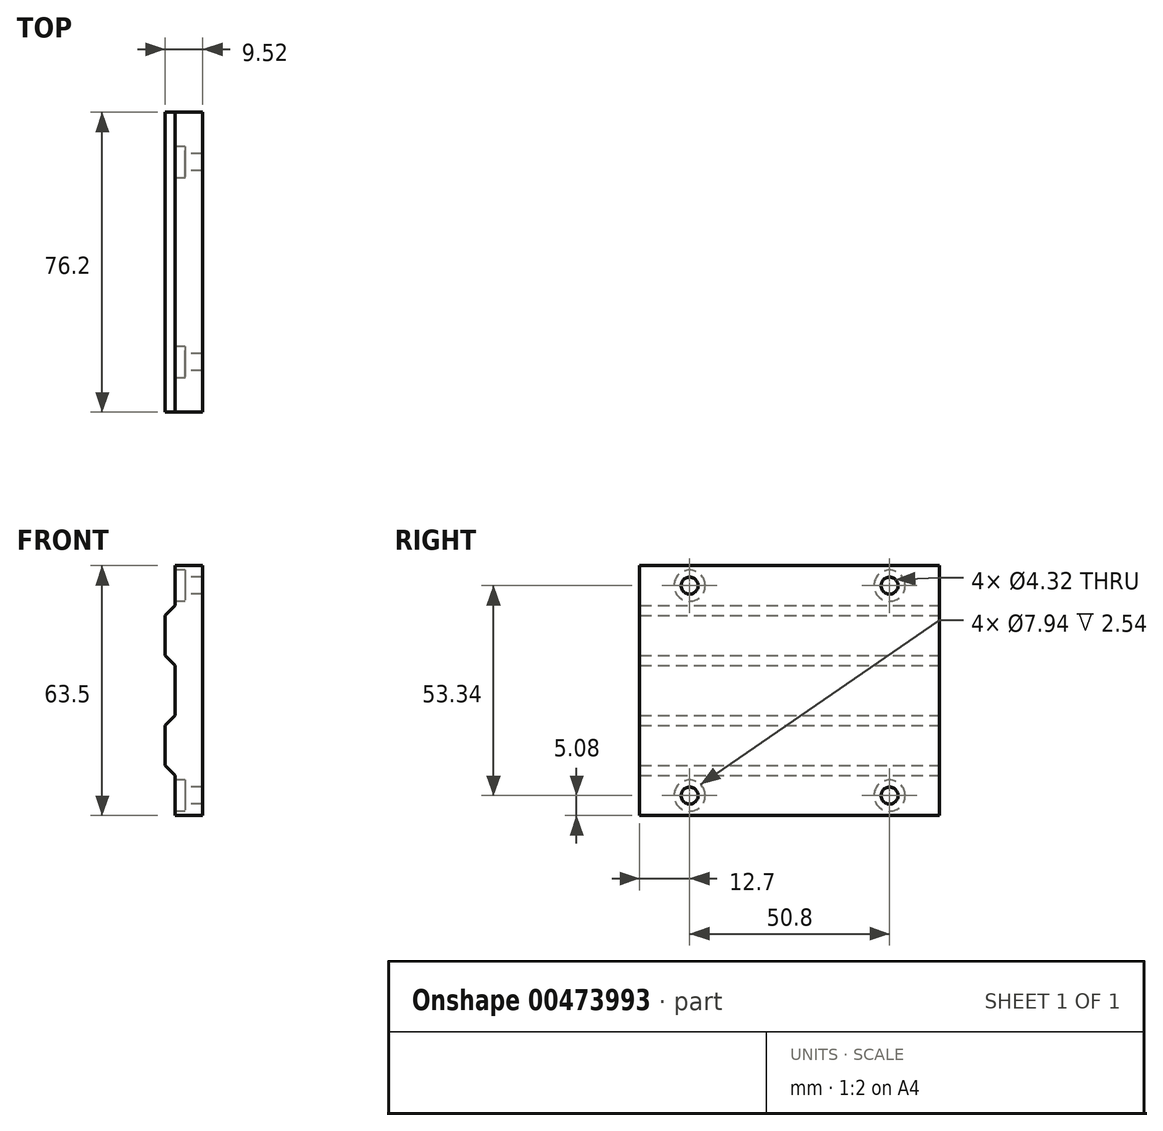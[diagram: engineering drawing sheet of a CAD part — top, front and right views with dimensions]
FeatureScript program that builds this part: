
annotation { "Feature Type Name" : "Feature", "Feature Type Description" : "" }
export const myFeature = defineFeature(function(context is Context, id is Id, definition is map)
    precondition{}
    {
        {
            var Q0;
            Q0=qCreatedBy(makeId("Front.planeOp"),FACE);
            var sketch = newSketch(context, id + "F0", { "sketchPlane" : qUnion([Q0])});
            skLineSegment(sketch, "E0.0.0", {"start": v(6.99, 40.64) * mm, "end": v(6.98, 50.8) * mm});
            skLineSegment(sketch, "E0.0.1", {"start": v(6.98, 50.8) * mm, "end": v(9.52, 53.34) * mm});
            skLineSegment(sketch, "E0.0.2", {"start": v(9.52, 53.34) * mm, "end": v(9.52, 63.5) * mm});
            skLineSegment(sketch, "E0.0.3", {"start": v(9.52, 63.5) * mm, "end": v(0, 63.5) * mm});
            skLineSegment(sketch, "E0.0.4", {"start": v(0, 63.5) * mm, "end": v(0, 0) * mm});
            skLineSegment(sketch, "E0.0.5", {"start": v(0, 0) * mm, "end": v(9.53, 0) * mm});
            skLineSegment(sketch, "E0.0.6", {"start": v(9.53, 0) * mm, "end": v(9.53, 10.16) * mm});
            skLineSegment(sketch, "E0.0.7", {"start": v(9.53, 10.16) * mm, "end": v(6.98, 12.7) * mm});
            skLineSegment(sketch, "E0.0.8", {"start": v(6.99, 12.7) * mm, "end": v(6.98, 22.86) * mm});
            skLineSegment(sketch, "E0.0.9", {"start": v(6.98, 22.86) * mm, "end": v(9.52, 25.4) * mm});
            skLineSegment(sketch, "E0.0.10", {"start": v(9.53, 25.4) * mm, "end": v(9.52, 38.1) * mm});
            skLineSegment(sketch, "E0.0.11", {"start": v(9.52, 38.1) * mm, "end": v(6.98, 40.64) * mm});
            skLineSegment(sketch, "E1", {"start": v(9.52, 63.5) * mm, "end": v(16.5, 63.5) * mm});
            skLineSegment(sketch, "E2", {"start": v(16.5, 63.5) * mm, "end": v(16.51, 0) * mm});
            skLineSegment(sketch, "E3", {"start": v(16.51, 0) * mm, "end": v(9.53, 0) * mm});
            skSolve(sketch);
        }
        {
            var Q0;
            Q0=makeQuery(id+"F0.imprint","IMPRINT",FACE,{"disambiguationData":[TD([[makeQuery(id+"F0.imprint","IMPRINT",EDGE,{"derivedFrom":sQuery(id+"F0.wireOp",EDGE,"E0.0.0")}),-1.0]])]});
            extrude(context, id + "F1", {"entities" : qUnion([Q0]), "depth" : 76.2 * mm});
        }
        {
            var Q0;
            Q0=makeQuery(id+"F1.opExtrude","SWEPT_FACE",FACE,{"disambiguationData":[OSD([sQuery(id+"F0.wireOp",EDGE,"E0.0.2")])]});
            var sketch = newSketch(context, id + "F2", { "sketchPlane" : qUnion([Q0])});
            skPoint(sketch, "E4", {"position": v(12.7, 58.42) * mm});
            skPoint(sketch, "E5", {"position": v(63.5, 58.42) * mm});
            skPoint(sketch, "E6", {"position": v(12.7, 5.08) * mm});
            skPoint(sketch, "E7", {"position": v(63.5, 5.08) * mm});
            skSolve(sketch);
        }
        {
            var Q0;
            Q0=sQuery(id+"F2.wireOp",VERTEX,"E6");
            var Q1;
            Q1=sQuery(id+"F2.wireOp",VERTEX,"E7");
            var Q2;
            Q2=makeQuery(id+"F1.opExtrude","SWEPT_BODY",BODY,{"disambiguationData":[OSD([sQuery(id+"F0.wireOp",EDGE,"E0.0.0"),sQuery(id+"F0.wireOp",EDGE,"E0.0.1"),sQuery(id+"F0.wireOp",EDGE,"E0.0.2"),sQuery(id+"F0.wireOp",EDGE,"E0.0.6"),sQuery(id+"F0.wireOp",EDGE,"E0.0.7"),sQuery(id+"F0.wireOp",EDGE,"E0.0.8"),sQuery(id+"F0.wireOp",EDGE,"E0.0.9"),sQuery(id+"F0.wireOp",EDGE,"E0.0.10"),sQuery(id+"F0.wireOp",EDGE,"E0.0.11"),sQuery(id+"F0.wireOp",EDGE,"E1"),sQuery(id+"F0.wireOp",EDGE,"E2"),sQuery(id+"F0.wireOp",EDGE,"E3")])]});
            hole(context, id + "F3", {"style" : HoleStyle.SIMPLE, "endStyle" : HoleEndStyle.BLIND, "standardTappedOrClearance" : lookupTablePath({ "standard" : "ANSI", "fit" : "Close", "size" : "#8", "type" : "Clearance" }), "standardBlindInLast" : lookupTablePath({ "fit" : "Close", "standard" : "ANSI", "size" : "#8", "type" : "Clearance" }), "holeDiameter" : 4.32 * mm, "holeDepth" : 12.7 * mm, "isTappedThrough" : true, "tappedDepth" : 10.32 * mm, "tapClearance" : 3, "locations" : qUnion([Q0, Q1]), "scope" : qUnion([Q2]), "majorDiameter" : 6.35 * mm});
        }
        {
            var Q0;
            Q0=makeQuery(id+"F1.opExtrude","SWEPT_FACE",FACE,{"disambiguationData":[OSD([sQuery(id+"F0.wireOp",EDGE,"E2")])]});
            var sketch = newSketch(context, id + "F4", { "sketchPlane" : qUnion([Q0])});
            skSolve(sketch);
        }
        {
            var Q0;
            Q0=makeQuery(id+"F1.opExtrude","SWEPT_FACE",FACE,{"disambiguationData":[OSD([sQuery(id+"F0.wireOp",EDGE,"E0.0.6")])]});
            var sketch = newSketch(context, id + "F5", { "sketchPlane" : qUnion([Q0])});
            skCircle(sketch, "E8.0", {"center": v(12.7, 5.08) * mm, "radius": 2.16 * mm});
            skCircle(sketch, "E9.0.0", {"center": v(63.5, 5.08) * mm, "radius": 2.16 * mm});
            skCircle(sketch, "E10", {"center": v(12.7, 5.08) * mm, "radius": 3.97 * mm});
            skCircle(sketch, "E11", {"center": v(63.5, 5.08) * mm, "radius": 3.97 * mm});
            skSolve(sketch);
        }
        {
            var Q0;
            Q0=makeQuery(id+"F5.imprint","IMPRINT",FACE,{"disambiguationData":[TD([[makeQuery(id+"F5.imprint","IMPRINT",EDGE,{"derivedFrom":sQuery(id+"F5.wireOp",EDGE,"E9.0.0")}),-1.0]])]});
            var Q1;
            Q1=makeQuery(id+"F5.imprint","IMPRINT",FACE,{"disambiguationData":[TD([[makeQuery(id+"F5.imprint","IMPRINT",EDGE,{"derivedFrom":sQuery(id+"F5.wireOp",EDGE,"E8.0")}),-1.0]])]});
            extrude(context, id + "F6", {"entities" : qUnion([Q0, Q1]), "operationType" : NewBodyOperationType.REMOVE, "oppositeDirection" : true, "depth" : 2.54 * mm, "offsetDistance" : 25.4 * mm});
        }
        {
            var Q0;
            Q0=makeQuery(id+"F1.opExtrude","SWEPT_FACE",FACE,{"disambiguationData":[OSD([sQuery(id+"F0.wireOp",EDGE,"E0.0.2")])]});
            var sketch = newSketch(context, id + "F7", { "sketchPlane" : qUnion([Q0])});
            skPoint(sketch, "E12", {"position": v(12.7, 58.42) * mm});
            skPoint(sketch, "E13", {"position": v(63.5, 58.42) * mm});
            skCircle(sketch, "E14.0.0", {"center": v(12.7, 5.08) * mm, "radius": 2.16 * mm});
            skCircle(sketch, "E15.0.0", {"center": v(63.5, 5.08) * mm, "radius": 2.16 * mm});
            skSolve(sketch);
        }
        {
            var Q0;
            Q0=sQuery(id+"F7.wireOp",VERTEX,"E12");
            var Q1;
            Q1=sQuery(id+"F7.wireOp",VERTEX,"E13");
            var Q2;
            Q2=makeQuery(id+"F1.opExtrude","SWEPT_BODY",BODY,{"disambiguationData":[OSD([sQuery(id+"F0.wireOp",EDGE,"E0.0.0"),sQuery(id+"F0.wireOp",EDGE,"E0.0.1"),sQuery(id+"F0.wireOp",EDGE,"E0.0.2"),sQuery(id+"F0.wireOp",EDGE,"E0.0.6"),sQuery(id+"F0.wireOp",EDGE,"E0.0.7"),sQuery(id+"F0.wireOp",EDGE,"E0.0.8"),sQuery(id+"F0.wireOp",EDGE,"E0.0.9"),sQuery(id+"F0.wireOp",EDGE,"E0.0.10"),sQuery(id+"F0.wireOp",EDGE,"E0.0.11"),sQuery(id+"F0.wireOp",EDGE,"E1"),sQuery(id+"F0.wireOp",EDGE,"E2"),sQuery(id+"F0.wireOp",EDGE,"E3")])]});
            hole(context, id + "F8", {"style" : HoleStyle.SIMPLE, "endStyle" : HoleEndStyle.BLIND, "standardTappedOrClearance" : lookupTablePath({ "standard" : "ANSI", "fit" : "Close", "size" : "#8", "type" : "Clearance" }), "standardBlindInLast" : lookupTablePath({ "fit" : "Close", "standard" : "ANSI", "size" : "#8", "type" : "Clearance" }), "holeDiameter" : 4.32 * mm, "majorDiameter" : 6.35 * mm, "holeDepth" : 12.7 * mm, "isTappedThrough" : true, "tappedDepth" : 10.32 * mm, "tapClearance" : 3, "locations" : qUnion([Q0, Q1]), "scope" : qUnion([Q2])});
        }
        {
            var Q0;
            Q0=makeQuery(id+"F1.opExtrude","SWEPT_FACE",FACE,{"disambiguationData":[OSD([sQuery(id+"F0.wireOp",EDGE,"E0.0.2")])]});
            var sketch = newSketch(context, id + "F9", { "sketchPlane" : qUnion([Q0])});
            skCircle(sketch, "E16.0", {"center": v(12.7, 58.42) * mm, "radius": 2.16 * mm});
            skCircle(sketch, "E17.0", {"center": v(63.5, 58.42) * mm, "radius": 2.16 * mm});
            skCircle(sketch, "E18", {"center": v(12.7, 58.42) * mm, "radius": 3.97 * mm});
            skCircle(sketch, "E19", {"center": v(63.5, 58.42) * mm, "radius": 3.97 * mm});
            skSolve(sketch);
        }
        {
            var Q0;
            Q0=makeQuery(id+"F9.imprint","IMPRINT",FACE,{"disambiguationData":[TD([[makeQuery(id+"F9.imprint","IMPRINT",EDGE,{"derivedFrom":sQuery(id+"F9.wireOp",EDGE,"E16.0")}),-1.0]])]});
            var Q1;
            Q1=makeQuery(id+"F9.imprint","IMPRINT",FACE,{"disambiguationData":[TD([[makeQuery(id+"F9.imprint","IMPRINT",EDGE,{"derivedFrom":sQuery(id+"F9.wireOp",EDGE,"E17.0")}),-1.0]])]});
            extrude(context, id + "F10", {"entities" : qUnion([Q0, Q1]), "operationType" : NewBodyOperationType.REMOVE, "oppositeDirection" : true, "depth" : 2.54 * mm, "offsetDistance" : 25.4 * mm});
        }
    });
